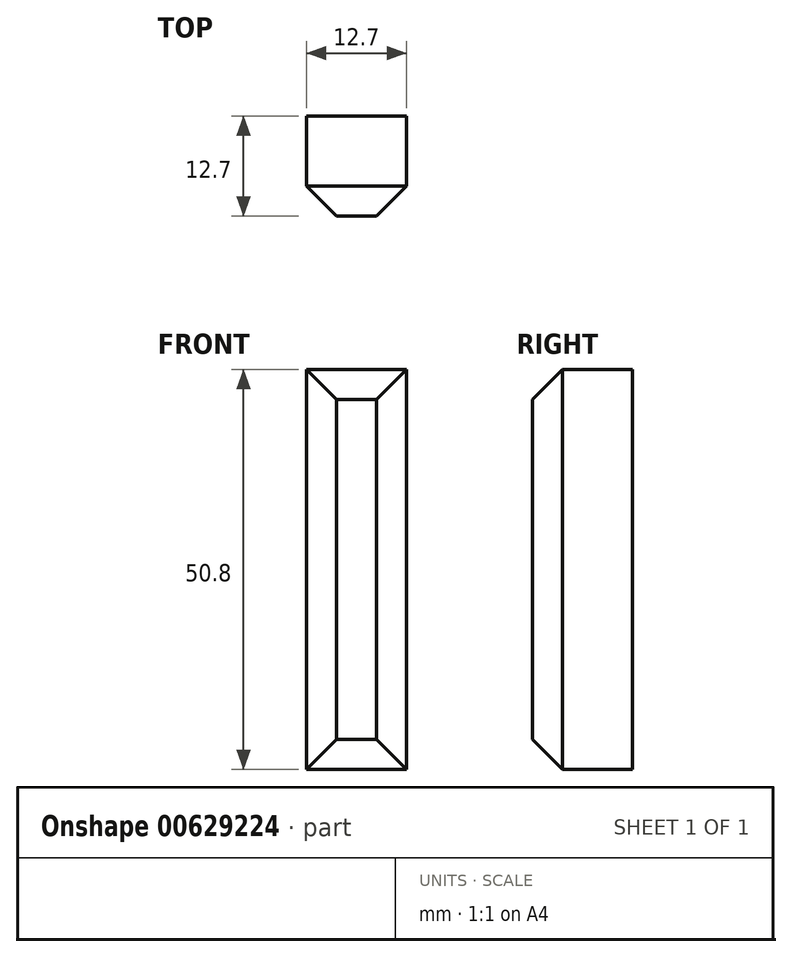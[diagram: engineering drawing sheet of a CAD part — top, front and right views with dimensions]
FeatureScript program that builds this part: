
annotation { "Feature Type Name" : "Feature", "Feature Type Description" : "" }
export const myFeature = defineFeature(function(context is Context, id is Id, definition is map)
    precondition{}
    {
        {
            var Q0;
            Q0=qCreatedBy(makeId("Front.planeOp"),FACE);
            var sketch = newSketch(context, id + "F0", { "sketchPlane" : qUnion([Q0])});
            skLineSegment(sketch, "E0.bottom", {"start": v(0, 0) * mm, "end": v(-12.7, 0) * mm});
            skLineSegment(sketch, "E0.top", {"start": v(0, 50.8) * mm, "end": v(-12.7, 50.8) * mm});
            skLineSegment(sketch, "E0.left", {"start": v(0, 0) * mm, "end": v(0, 50.8) * mm});
            skLineSegment(sketch, "E0.right", {"start": v(-12.7, 0) * mm, "end": v(-12.7, 50.8) * mm});
            skSolve(sketch);
        }
        {
            var Q0;
            Q0=makeQuery(id+"F0.imprint","IMPRINT",FACE,{"disambiguationData":[TD([[makeQuery(id+"F0.imprint","IMPRINT",EDGE,{"derivedFrom":sQuery(id+"F0.wireOp",EDGE,"E0.bottom")}),-1.0]])]});
            extrude(context, id + "F1", {"entities" : qUnion([Q0]), "depth" : 12.7 * mm, "offsetDistance" : 25.4 * mm});
        }
        {
            var Q0;
            Q0=makeQuery(id+"F1.opExtrude","CAP_FACE",FACE,{"disambiguationData":[OSD([sQuery(id+"F0.wireOp",EDGE,"E0.bottom"),sQuery(id+"F0.wireOp",EDGE,"E0.top"),sQuery(id+"F0.wireOp",EDGE,"E0.left"),sQuery(id+"F0.wireOp",EDGE,"E0.right")])],"isStart":false});
            chamfer(context, id + "F2", {"entities" : qUnion([Q0]), "width" : 3.8 * mm, "tangentPropagation" : true});
        }
    });
